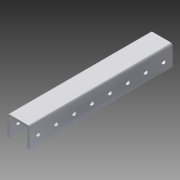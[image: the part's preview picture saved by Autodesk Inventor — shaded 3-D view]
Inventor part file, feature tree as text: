
AUTODESK INVENTOR PART (.ipt)
format: ipt  version: 2015 (Build 190159000, 159)  size: 186,880 bytes
history: native  units: in
note: dims shown in document units (in); Inventor stores cm internally (conversion verified against a paired STEP export)
features: extrude x2, sketch x2, pattern_linear x1
ambient origin geometry x8: Origin, YZ Plane, XZ Plane, XY Plane, X Axis, Y Axis, Z Axis, Center Point
bodies: Solid1 (feature_tree)
feature tree (5):
  extrude  "Extrusion1"  Depth=8.0in
  extrude  "Extrusion4"  Depth=0.5in
  pattern_linear  "Rectangular Pattern3"  Spacing1=0.5in  [1 undecoded]
  sketch  "Sketch1"  dims[d0=1.13in d1=1.25in d2=0.125in d3=0.125in d4=0.125in d5=8.0in]
  sketch  "Sketch4"  dims[d6=0.0in d34=0.5in d35=0.5in d36=0.25in d37=1.0in d38=0.0in d39=5.9055in d41=1.0in d42=5.9055in d44=1.0in]
note: 1 required parameter value undecoded (feature->parameter linkage not recoverable at this tier; creation-order binding heuristic only, values carry confidence <= 0.55)
